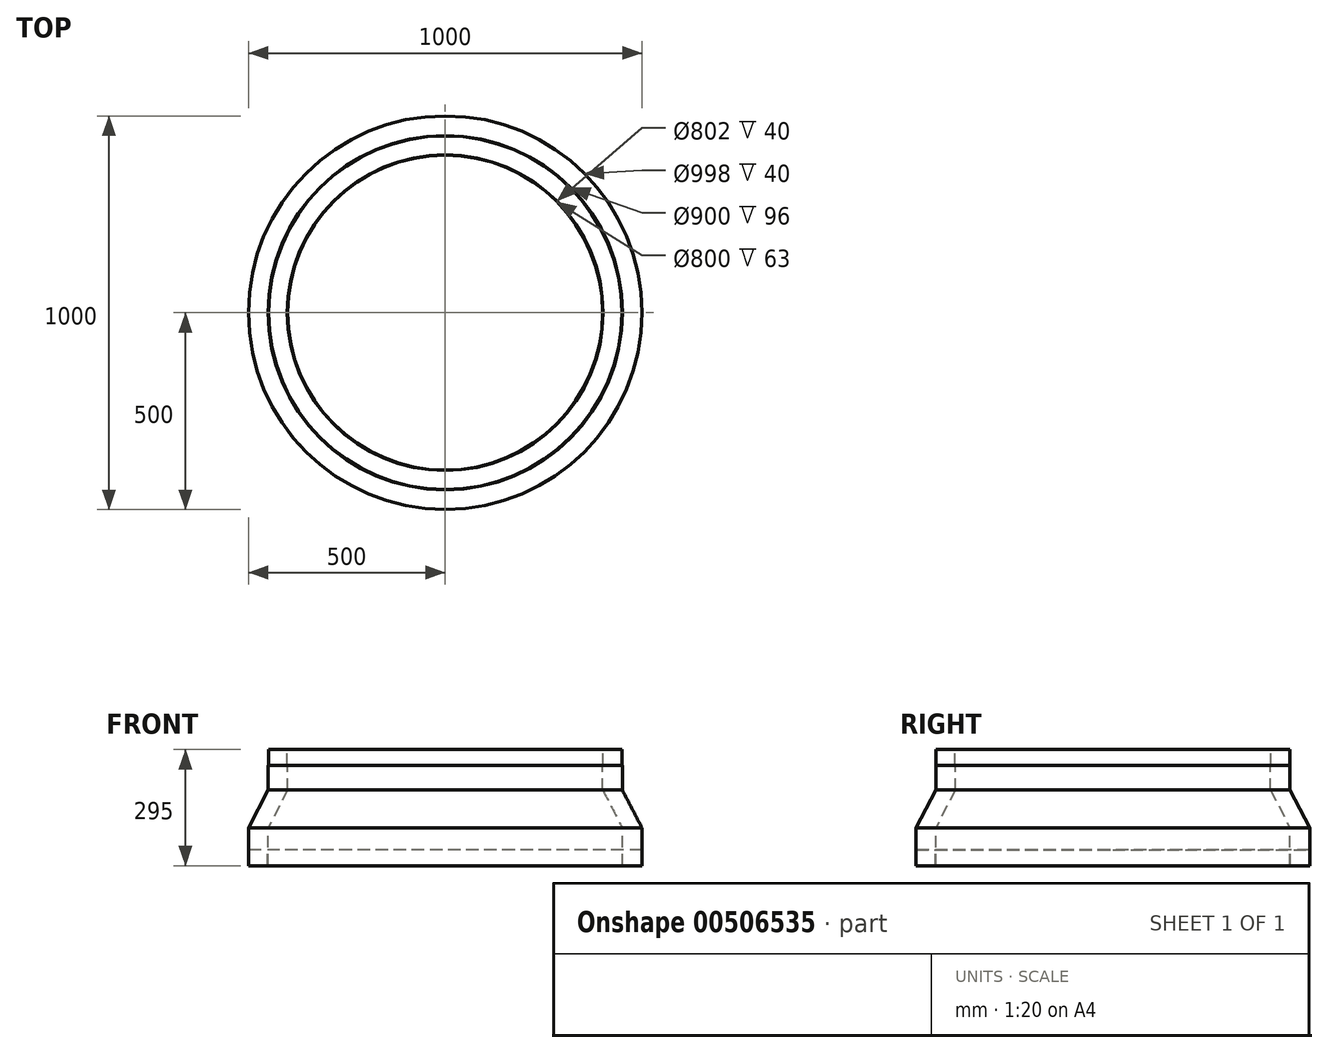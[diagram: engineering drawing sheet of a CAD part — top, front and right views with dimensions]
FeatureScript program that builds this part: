
annotation { "Feature Type Name" : "Feature", "Feature Type Description" : "" }
export const myFeature = defineFeature(function(context is Context, id is Id, definition is map)
    precondition{}
    {
        {
            var Q0;
            Q0=qCreatedBy(makeId("Front.planeOp"),FACE);
            var sketch = newSketch(context, id + "F0", { "sketchPlane" : qUnion([Q0])});
            skLineSegment(sketch, "E0", {"start": v(0, 433.08) * mm, "end": v(0, -434.74) * mm, "construction": true});
            skLineSegment(sketch, "E1", {"start": v(-450, -258.87) * mm, "end": v(-450, -162.87) * mm});
            skLineSegment(sketch, "E2", {"start": v(-450, -258.87) * mm, "end": v(-451, -258.87) * mm});
            skLineSegment(sketch, "E3", {"start": v(-451, -258.87) * mm, "end": v(-451, -218.87) * mm});
            skLineSegment(sketch, "E4", {"start": v(-451, -218.87) * mm, "end": v(-499, -218.87) * mm});
            skLineSegment(sketch, "E5", {"start": v(-499, -218.87) * mm, "end": v(-499, -258.87) * mm});
            skLineSegment(sketch, "E6", {"start": v(-499, -258.87) * mm, "end": v(-500, -258.87) * mm});
            skLineSegment(sketch, "E7", {"start": v(-500, -258.87) * mm, "end": v(-500, -162.87) * mm});
            skLineSegment(sketch, "E8", {"start": v(-449, 36.13) * mm, "end": v(-401, 36.13) * mm});
            skLineSegment(sketch, "E9", {"start": v(-401, 36.13) * mm, "end": v(-401, -3.87) * mm});
            skLineSegment(sketch, "E10", {"start": v(-401, -3.87) * mm, "end": v(-400, -3.87) * mm});
            skLineSegment(sketch, "E11", {"start": v(-400, -3.87) * mm, "end": v(-400, -66.87) * mm});
            skLineSegment(sketch, "E12", {"start": v(-449, 36.13) * mm, "end": v(-449, -3.87) * mm});
            skLineSegment(sketch, "E13", {"start": v(-449, -3.87) * mm, "end": v(-450, -3.87) * mm});
            skLineSegment(sketch, "E14", {"start": v(-450, -3.87) * mm, "end": v(-450, -66.87) * mm});
            skLineSegment(sketch, "E15", {"start": v(-400, -66.87) * mm, "end": v(-450, -162.87) * mm});
            skLineSegment(sketch, "E16", {"start": v(-450, -66.87) * mm, "end": v(-500, -162.87) * mm});
            skSolve(sketch);
        }
        {
            var Q0;
            Q0=qSketchRegion(id+"F0",true);
            var Q1;
            Q1=sQuery(id+"F0.wireOp",EDGE,"E0");
            revolve(context, id + "F1", {"entities" : qUnion([Q0]), "axis" : qUnion([Q1]), "revolveType" : RevolveType.FULL});
        }
    });
